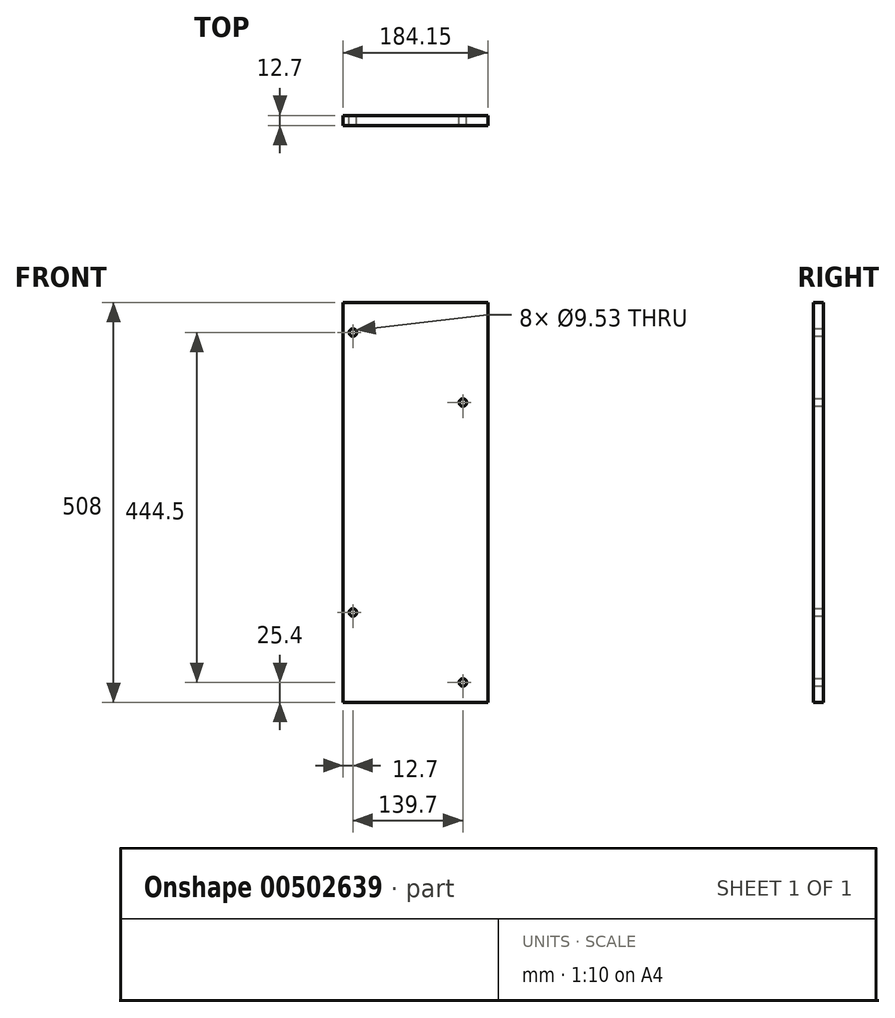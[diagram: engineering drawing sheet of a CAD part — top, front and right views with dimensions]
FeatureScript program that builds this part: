
annotation { "Feature Type Name" : "Feature", "Feature Type Description" : "" }
export const myFeature = defineFeature(function(context is Context, id is Id, definition is map)
    precondition{}
    {
        {
            var Q0;
            Q0=qCreatedBy(makeId("Front.planeOp"),FACE);
            var sketch = newSketch(context, id + "F0", { "sketchPlane" : qUnion([Q0])});
            skLineSegment(sketch, "E0.bottom", {"start": v(0, 0) * mm, "end": v(184.15, 0) * mm});
            skLineSegment(sketch, "E0.top", {"start": v(0, 508) * mm, "end": v(184.15, 508) * mm});
            skLineSegment(sketch, "E0.left", {"start": v(0, 0) * mm, "end": v(0, 508) * mm});
            skLineSegment(sketch, "E0.right", {"start": v(184.15, 0) * mm, "end": v(184.15, 508) * mm});
            skCircle(sketch, "E1", {"center": v(152.4, 25.4) * mm, "radius": 4.76 * mm});
            skCircle(sketch, "E2", {"center": v(152.4, 381) * mm, "radius": 4.76 * mm});
            skCircle(sketch, "E3", {"center": v(12.7, 469.9) * mm, "radius": 4.76 * mm});
            skCircle(sketch, "E4", {"center": v(12.7, 114.3) * mm, "radius": 4.76 * mm});
            skSolve(sketch);
        }
        {
            var Q0;
            Q0=makeQuery(id+"F0.imprint","IMPRINT",FACE,{"disambiguationData":[TD([[makeQuery(id+"F0.imprint","IMPRINT",EDGE,{"derivedFrom":sQuery(id+"F0.wireOp",EDGE,"E0.bottom")}),1.0]])]});
            extrude(context, id + "F1", {"entities" : qUnion([Q0]), "depth" : 12.7 * mm});
        }
    });
